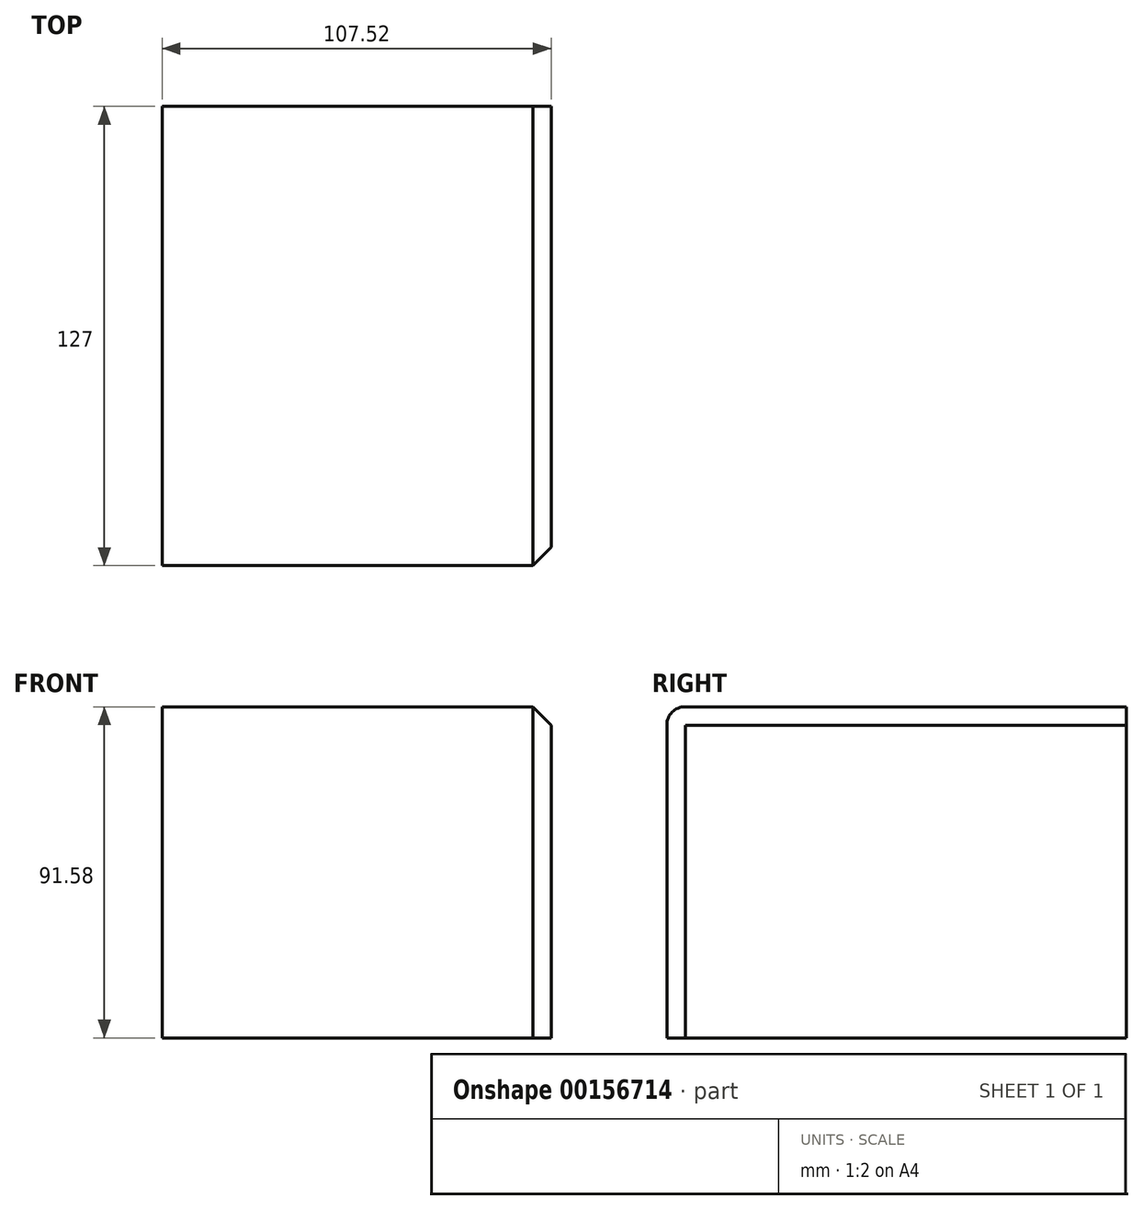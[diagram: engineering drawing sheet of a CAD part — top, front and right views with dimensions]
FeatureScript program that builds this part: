
annotation { "Feature Type Name" : "Feature", "Feature Type Description" : "" }
export const myFeature = defineFeature(function(context is Context, id is Id, definition is map)
    precondition{}
    {
        {
            var Q0;
            Q0=qCreatedBy(makeId("Front.planeOp"),FACE);
            var sketch = newSketch(context, id + "F0", { "sketchPlane" : qUnion([Q0])});
            skLineSegment(sketch, "E0.bottom", {"start": v(-50, 50) * mm, "end": v(57.5, 50) * mm});
            skLineSegment(sketch, "E0.top", {"start": v(-50, -41.57) * mm, "end": v(57.5, -41.57) * mm});
            skLineSegment(sketch, "E0.left", {"start": v(-50, 50) * mm, "end": v(-50, -41.57) * mm});
            skLineSegment(sketch, "E0.right", {"start": v(57.5, 50) * mm, "end": v(57.5, -41.57) * mm});
            skSolve(sketch);
        }
        {
            var Q0;
            Q0=makeQuery(id+"F0.imprint","IMPRINT",FACE,{"disambiguationData":[TD([[makeQuery(id+"F0.imprint","IMPRINT",EDGE,{"derivedFrom":sQuery(id+"F0.wireOp",EDGE,"E0.bottom")}),-1.0]])]});
            extrude(context, id + "F1", {"entities" : qUnion([Q0]), "oppositeDirection" : true, "depth" : 127 * mm});
        }
        {
            var Q0;
            Q0=makeQuery(id+"F1.opExtrude","CAP_EDGE",EDGE,{"disambiguationData":[OSD([sQuery(id+"F0.wireOp",EDGE,"E0.bottom")])],"isStart":true});
            fillet(context, id + "F2", {"entities" : qUnion([Q0]), "radius" : 5.08 * mm, "tangentPropagation" : true, "allowEdgeOverflow" : false});
        }
        {
            var Q0;
            Q0=makeQuery(id+"F1.opExtrude","SWEPT_EDGE",EDGE,{"disambiguationData":[OSD([sQuery(id+"F0.wireOp",EDGE,"E0.bottom"),sQuery(id+"F0.wireOp",EDGE,"E0.right")])]});
            chamfer(context, id + "F3", {"entities" : qUnion([Q0]), "width" : 5.08 * mm, "tangentPropagation" : true});
        }
    });
